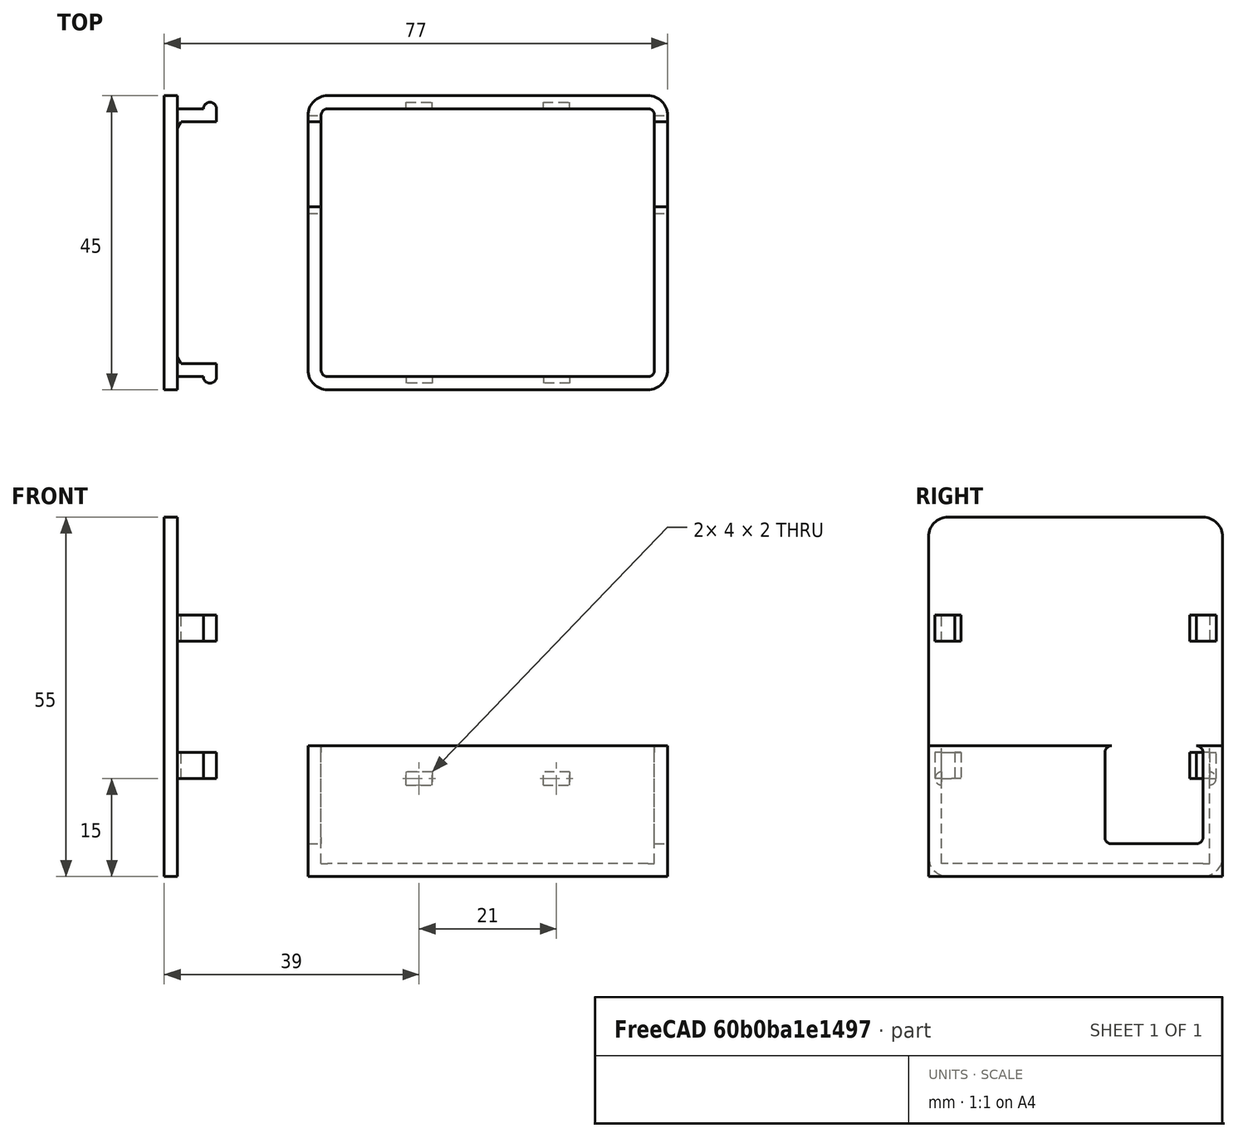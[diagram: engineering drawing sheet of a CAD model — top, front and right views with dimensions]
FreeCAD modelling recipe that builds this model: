
FCSTD DOCUMENT  (FreeCAD 0.15R4671 (Git))
Label: small_box
License: All rights reserved
LicenseURL: http://en.wikipedia.org/wiki/All_rights_reserved
objects: Part::FeaturePython×7, Part::Cut×5, Part::Box×4, Part::Fillet×3, Part::MultiFuse×3, Part::Thickness×1, Part::Cylinder×1, Part::Prism×1
note: 25 computed .brp shape members not serialized (recipe doc carries the construction recipe); baked Part::Feature solids carry a one-line shape summary decoded from their .brp

FEATURE [Part::Box] Box  label="Cube"
  Height = 2
  Length = 55
  Width = 45
FEATURE [Part::Fillet] Fillet
  Base = -> Box
  Edges = 4 edges r=3: [Edge1,Edge3,Edge5,Edge7]
  Placement = pos=(0,0,20) rot=(0,0,1;0rad)
FEATURE [Part::Box] Box001  label="Cube001"
  Height = 20
  Length = 55
  Width = 45
FEATURE [Part::Fillet] Fillet001
  Base = -> Box001
  Edges = 4 edges r=3: [Edge1,Edge3,Edge5,Edge7]
FEATURE [Part::Thickness] Thickness
  Faces = -> Fillet001 [Face2]
  Intersection = false
  Join = 0
  Mode = 0
  SelfIntersection = false
  Value = -2
FEATURE [Part::Box] Box002  label="Cube002"
  Height = 15
  Length = 60
  Placement = pos=(-2,27,5) rot=(0,0,1;0rad)
  Width = 15
FEATURE [Part::Fillet] Fillet002
  Base = -> Box002
  Edges = 4 edges r=1: [Edge9,Edge10,Edge11,Edge12]
FEATURE [Part::Cut] Cut
  Base = -> Thickness
  Tool = -> Fillet002
FEATURE [Part::Box] Box003  label="Cube003"
  Height = 6
  Length = 2
  Width = 4
FEATURE [Part::Cylinder] Cylinder
  Angle = 360
  Height = 4
  Placement = pos=(0,4,5) rot=(1,0,0;1.5708rad)
  Radius = 1
FEATURE [Part::MultiFuse] Fusion
  Shapes = -> [Cylinder,Box003]
FEATURE [Part::Prism] Prism
  Circumradius = 1
  Height = 4
  Placement = pos=(2,4,0) rot=(1,0,0;1.5708rad)
  Polygon = 3
FEATURE [Part::MultiFuse] Fusion001  label="flange01"
  Placement = pos=(15,2,20) rot=(0.707107,0.707107,0;3.14159rad)
  Shapes = -> [Prism,Fusion]
FEATURE [Part::FeaturePython] Clone  label="flange02"  # Draft clone (typed FeaturePython)
  Objects = -> [Fusion001]
  Placement = pos=(36,2,20) rot=(0.707107,0.707107,0;3.14159rad)
  Scale = (1,1,1)
FEATURE [Part::FeaturePython] Clone001  label="flange03"  # Draft clone (typed FeaturePython)
  Objects = -> [Fusion001]
  Placement = pos=(19,43,20) rot=(-0.707107,0.707107,0;3.14159rad)
  Scale = (1,1,1)
FEATURE [Part::FeaturePython] Clone002  label="flange04"  # Draft clone (typed FeaturePython)
  Objects = -> [Clone]
  Placement = pos=(40,43,20) rot=(-0.707107,0.707107,0;3.14159rad)
  Scale = (1,1,1)
FEATURE [Part::FeaturePython] Clone003  label="Clone of flange01"  # Draft clone (typed FeaturePython)
  Objects = -> [Fusion001]
  Placement = pos=(15,2,20) rot=(0.707107,0.707107,0;3.14159rad)
  Scale = (1,1,1)
FEATURE [Part::FeaturePython] Clone004  label="Clone of flange04"  # Draft clone (typed FeaturePython)
  Objects = -> [Clone002]
  Placement = pos=(40,43,20) rot=(-0.707107,0.707107,0;3.14159rad)
  Scale = (1,1,1)
FEATURE [Part::FeaturePython] Clone005  label="Clone of flange02"  # Draft clone (typed FeaturePython)
  Objects = -> [Clone]
  Placement = pos=(36,2,20) rot=(0.707107,0.707107,0;3.14159rad)
  Scale = (1,1,1)
FEATURE [Part::FeaturePython] Clone006  label="Clone of flange03"  # Draft clone (typed FeaturePython)
  Objects = -> [Clone001]
  Placement = pos=(19,43,20) rot=(-0.707107,0.707107,0;3.14159rad)
  Scale = (1,1,1)
FEATURE [Part::MultiFuse] Fusion002  label="top"
  Placement = pos=(0,0,0) rot=(0,1,0;4.71239rad)
  Shapes = -> [Fillet,Fusion001,Clone,Clone001,Clone002]
FEATURE [Part::Cut] Cut001
  Base = -> Cut
  Tool = -> Clone003
FEATURE [Part::Cut] Cut002
  Base = -> Cut001
  Tool = -> Clone004
FEATURE [Part::Cut] Cut003
  Base = -> Cut002
  Tool = -> Clone005
FEATURE [Part::Cut] Cut004  label="case"
  Base = -> Cut003
  Tool = -> Clone006
